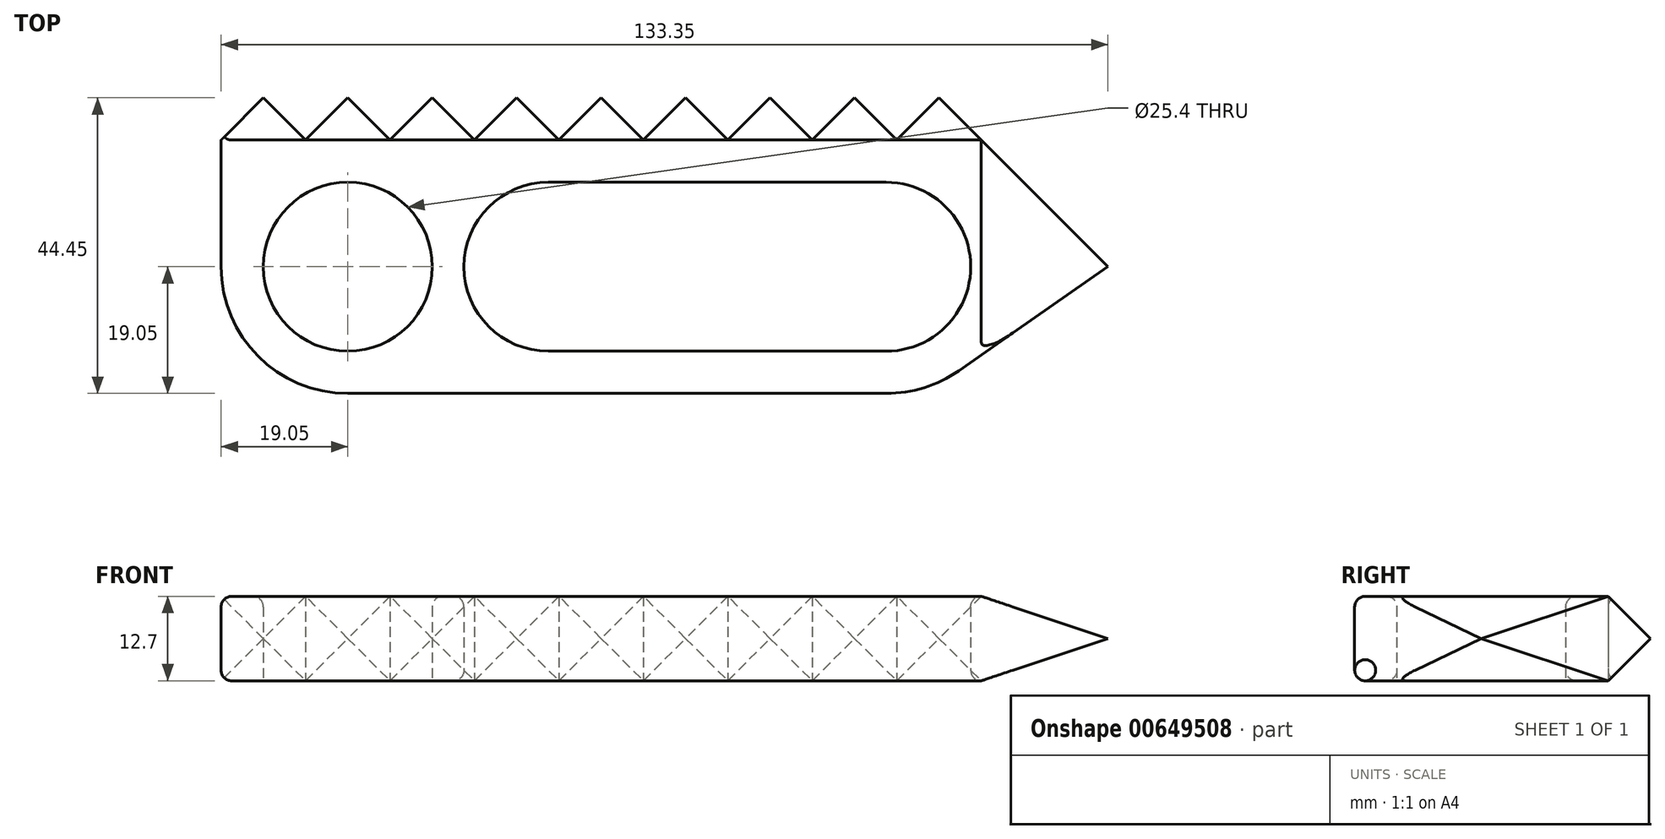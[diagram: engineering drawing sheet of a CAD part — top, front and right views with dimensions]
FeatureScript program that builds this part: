
annotation { "Feature Type Name" : "Feature", "Feature Type Description" : "" }
export const myFeature = defineFeature(function(context is Context, id is Id, definition is map)
    precondition{}
    {
        {
            var Q0;
            Q0=qCreatedBy(makeId("Top.planeOp"),FACE);
            var sketch = newSketch(context, id + "F0", { "sketchPlane" : qUnion([Q0])});
            skCircle(sketch, "E0", {"center": v(0, 0) * mm, "radius": 12.7 * mm});
            skArc(sketch, "E1", {"start": v(30.15, 12.7) * mm, "mid": v(17.46, 0) * mm, "end": v(30.15, -12.7) * mm});
            skLineSegment(sketch, "E2", {"start": v(30.15, 12.7) * mm, "end": v(80.95, 12.7) * mm});
            skLineSegment(sketch, "E3", {"start": v(30.15, -12.7) * mm, "end": v(80.95, -12.7) * mm});
            skArc(sketch, "E4", {"start": v(80.95, -12.7) * mm, "mid": v(93.66, 0) * mm, "end": v(80.95, 12.7) * mm});
            skArc(sketch, "E5", {"start": v(0, -19.05) * mm, "mid": v(-13.47, -13.47) * mm, "end": v(-19.05, 0) * mm});
            skArc(sketch, "E6", {"start": v(80.96, -19.05) * mm, "mid": v(94.43, -13.47) * mm, "end": v(100.01, 0) * mm});
            skLineSegment(sketch, "E7", {"start": v(0, -19.05) * mm, "end": v(80.96, -19.05) * mm});
            skLineSegment(sketch, "E8", {"start": v(-19.05, 0) * mm, "end": v(-19.05, 25.4) * mm});
            skLineSegment(sketch, "E9", {"start": v(100.01, 0) * mm, "end": v(100.01, 25.4) * mm});
            skLineSegment(sketch, "E10", {"start": v(100.01, 25.4) * mm, "end": v(-19.05, 25.4) * mm});
            skLineSegment(sketch, "E11", {"start": v(-19.05, 19.05) * mm, "end": v(100.01, 19.05) * mm});
            skLineSegment(sketch, "E12", {"start": v(-12.7, 25.4) * mm, "end": v(-19.05, 19.05) * mm});
            skLineSegment(sketch, "E13", {"start": v(-12.7, 25.4) * mm, "end": v(-6.35, 19.05) * mm});
            skLineSegment(sketch, "E14", {"start": v(-6.35, 19.05) * mm, "end": v(0, 25.4) * mm});
            skLineSegment(sketch, "E15", {"start": v(0, 25.4) * mm, "end": v(6.35, 19.05) * mm});
            skLineSegment(sketch, "E16", {"start": v(6.35, 19.05) * mm, "end": v(12.7, 25.4) * mm});
            skLineSegment(sketch, "E17", {"start": v(12.7, 25.4) * mm, "end": v(12.7, 25.4) * mm});
            skLineSegment(sketch, "E18", {"start": v(12.7, 25.4) * mm, "end": v(19.05, 19.05) * mm});
            skLineSegment(sketch, "E19", {"start": v(19.05, 19.05) * mm, "end": v(25.4, 25.4) * mm});
            skLineSegment(sketch, "E20", {"start": v(25.4, 25.4) * mm, "end": v(31.75, 19.05) * mm});
            skLineSegment(sketch, "E21", {"start": v(31.75, 19.05) * mm, "end": v(38.1, 25.4) * mm});
            skPoint(sketch, "E21.endSnap0", {"position": v(40.48, 25.4) * mm});
            skLineSegment(sketch, "E22", {"start": v(38.1, 25.4) * mm, "end": v(44.45, 19.05) * mm});
            skLineSegment(sketch, "E23", {"start": v(44.45, 19.05) * mm, "end": v(50.8, 25.4) * mm});
            skLineSegment(sketch, "E24", {"start": v(50.8, 25.4) * mm, "end": v(57.15, 19.05) * mm});
            skLineSegment(sketch, "E25", {"start": v(57.15, 19.05) * mm, "end": v(63.5, 25.4) * mm});
            skLineSegment(sketch, "E26", {"start": v(63.5, 25.4) * mm, "end": v(69.85, 19.05) * mm});
            skLineSegment(sketch, "E27", {"start": v(69.85, 19.05) * mm, "end": v(76.2, 25.4) * mm});
            skLineSegment(sketch, "E28", {"start": v(76.2, 25.4) * mm, "end": v(82.55, 19.05) * mm});
            skLineSegment(sketch, "E29", {"start": v(82.55, 19.05) * mm, "end": v(88.9, 25.4) * mm});
            skLineSegment(sketch, "E30", {"start": v(88.9, 25.4) * mm, "end": v(114.3, 0) * mm});
            skLineSegment(sketch, "E31", {"start": v(114.3, 0) * mm, "end": v(91.85, -15.63) * mm});
            skSolve(sketch);
        }
        {
            var Q0;
            Q0 = qSketchRegion(id + "F0", true);
            extrude(context, id + "F1", {"entities" : qUnion([Q0]), "depth" : 12.7 * mm, "offsetDistance" : 25.4 * mm});
        }
        {
            var Q0;
            {var subQ0=sQuery(id+"F0.wireOp",EDGE,"E18");Q0=makeQuery(id+"F0.imprint","IMPRINT",FACE,{"disambiguationData":[TD([[makeQuery(id+"F0.imprint","IMPRINT",EDGE,{"derivedFrom":subQ0}),1.0]])]});}
            var Q1;
            {var subQ0=sQuery(id+"F0.wireOp",EDGE,"E22");Q1=makeQuery(id+"F0.imprint","IMPRINT",FACE,{"disambiguationData":[TD([[makeQuery(id+"F0.imprint","IMPRINT",EDGE,{"derivedFrom":subQ0}),1.0]])]});}
            var Q2;
            {var subQ3=sQuery(id+"F0.wireOp",EDGE,"E12");Q2=makeQuery(id+"F0.imprint","IMPRINT",FACE,{"disambiguationData":[TD([[makeQuery(id+"F0.imprint","IMPRINT",EDGE,{"derivedFrom":subQ3}),-1.0]])]});}
            var Q3;
            {var subQ0=sQuery(id+"F0.wireOp",EDGE,"E20");Q3=makeQuery(id+"F0.imprint","IMPRINT",FACE,{"disambiguationData":[TD([[makeQuery(id+"F0.imprint","IMPRINT",EDGE,{"derivedFrom":subQ0}),1.0]])]});}
            var Q4;
            {var subQ0=sQuery(id+"F0.wireOp",EDGE,"E10");var subQ1=sQuery(id+"F0.wireOp",EDGE,"E9");var subQ2=makeQuery(id+"F0.imprint","INTERSECT",VERTEX,{"derivedFrom":[subQ1,subQ0]});Q4=makeQuery(id+"F0.imprint","IMPRINT",FACE,{"disambiguationData":[TD([[makeQuery(id+"F0.imprint","IMPRINT",EDGE,{"disambiguationData":[TD([[subQ2,1.0]])],"derivedFrom":subQ1}),1.0]])]});}
            var Q5;
            {var subQ0=sQuery(id+"F0.wireOp",EDGE,"E28");Q5=makeQuery(id+"F0.imprint","IMPRINT",FACE,{"disambiguationData":[TD([[makeQuery(id+"F0.imprint","IMPRINT",EDGE,{"derivedFrom":subQ0}),1.0]])]});}
            var Q6;
            {var subQ0=sQuery(id+"F0.wireOp",EDGE,"E15");Q6=makeQuery(id+"F0.imprint","IMPRINT",FACE,{"disambiguationData":[TD([[makeQuery(id+"F0.imprint","IMPRINT",EDGE,{"derivedFrom":subQ0}),1.0]])]});}
            var Q7;
            {var subQ0=sQuery(id+"F0.wireOp",EDGE,"E24");Q7=makeQuery(id+"F0.imprint","IMPRINT",FACE,{"disambiguationData":[TD([[makeQuery(id+"F0.imprint","IMPRINT",EDGE,{"derivedFrom":subQ0}),1.0]])]});}
            var Q8;
            {var subQ0=sQuery(id+"F0.wireOp",EDGE,"E26");Q8=makeQuery(id+"F0.imprint","IMPRINT",FACE,{"disambiguationData":[TD([[makeQuery(id+"F0.imprint","IMPRINT",EDGE,{"derivedFrom":subQ0}),1.0]])]});}
            var Q9;
            {var subQ0=sQuery(id+"F0.wireOp",EDGE,"E13");Q9=makeQuery(id+"F0.imprint","IMPRINT",FACE,{"disambiguationData":[TD([[makeQuery(id+"F0.imprint","IMPRINT",EDGE,{"derivedFrom":subQ0}),1.0]])]});}
            var Q10;
            {var subQ0=sQuery(id+"F0.wireOp",EDGE,"E11");var subQ1=sQuery(id+"F0.wireOp",EDGE,"E9");var subQ2=makeQuery(id+"F0.imprint","INTERSECT",VERTEX,{"derivedFrom":[subQ1,subQ0]});Q10=makeQuery(id+"F0.imprint","IMPRINT",FACE,{"disambiguationData":[TD([[makeQuery(id+"F0.imprint","IMPRINT",EDGE,{"disambiguationData":[TD([[subQ2,1.0]])],"derivedFrom":subQ1}),1.0]])]});}
            extrude(context, id + "F2", {"entities" : qUnion([Q0, Q1, Q2, Q3, Q4, Q5, Q6, Q7, Q8, Q9, Q10]), "operationType" : NewBodyOperationType.REMOVE, "depth" : 25.4 * mm, "offsetDistance" : 25.4 * mm});
        }
        {
            var Q0;
            Q0=qCreatedBy(makeId("Right.planeOp"),FACE);
            var sketch = newSketch(context, id + "F3", { "sketchPlane" : qUnion([Q0])});
            skPoint(sketch, "E32", {"position": v(25.4, 0) * mm});
            skPoint(sketch, "E33", {"position": v(19.05, 0) * mm});
            skPoint(sketch, "E34", {"position": v(19.05, 12.7) * mm});
            skPoint(sketch, "E35", {"position": v(25.4, 12.7) * mm});
            skLineSegment(sketch, "E36", {"start": v(19.05, 0) * mm, "end": v(25.4, 6.35) * mm});
            skLineSegment(sketch, "E37", {"start": v(25.4, 6.35) * mm, "end": v(19.05, 12.7) * mm});
            skLineSegment(sketch, "E38", {"start": v(19.05, 12.7) * mm, "end": v(25.4, 12.7) * mm});
            skLineSegment(sketch, "E39", {"start": v(25.4, 12.7) * mm, "end": v(25.4, 0) * mm});
            skLineSegment(sketch, "E40", {"start": v(25.4, 0) * mm, "end": v(19.05, 0) * mm});
            skSolve(sketch);
        }
        {
            var Q0;
            Q0 = qSketchRegion(id + "F3", true);
            extrude(context, id + "F4", {"entities" : qUnion([Q0]), "operationType" : NewBodyOperationType.REMOVE, "depth" : 127 * mm, "offsetDistance" : 25.4 * mm, "hasSecondDirection" : true, "secondDirectionOppositeDirection" : true, "secondDirectionDepth" : 25.4 * mm});
        }
        {
            var Q0;
            Q0=qCreatedBy(makeId("Front.planeOp"),FACE);
            var sketch = newSketch(context, id + "F5", { "sketchPlane" : qUnion([Q0])});
            skPoint(sketch, "E41", {"position": v(95.25, 0) * mm});
            skPoint(sketch, "E42", {"position": v(95.25, 12.7) * mm});
            skPoint(sketch, "E43", {"position": v(114.3, 0) * mm});
            skPoint(sketch, "E44", {"position": v(114.3, 12.7) * mm});
            skLineSegment(sketch, "E45", {"start": v(95.25, 0) * mm, "end": v(114.3, 0) * mm});
            skLineSegment(sketch, "E46", {"start": v(114.3, 0) * mm, "end": v(114.3, 12.7) * mm});
            skLineSegment(sketch, "E47", {"start": v(114.3, 12.7) * mm, "end": v(95.25, 12.7) * mm});
            skLineSegment(sketch, "E48", {"start": v(95.25, 12.7) * mm, "end": v(114.3, 6.35) * mm});
            skLineSegment(sketch, "E49", {"start": v(114.3, 6.35) * mm, "end": v(95.25, 0) * mm});
            skSolve(sketch);
        }
        {
            var Q0;
            Q0 = qSketchRegion(id + "F5", true);
            extrude(context, id + "F6", {"entities" : qUnion([Q0]), "operationType" : NewBodyOperationType.REMOVE, "oppositeDirection" : true, "depth" : 50.8 * mm, "offsetDistance" : 25.4 * mm, "hasSecondDirection" : true, "secondDirectionOppositeDirection" : false, "secondDirectionDepth" : 25.4 * mm});
        }
        {
            var Q0;
            Q0=makeQuery(id+"F1.opExtrude","SWEPT_FACE",FACE,{"disambiguationData":[OSD([sQuery(id+"F0.wireOp",EDGE,"E2")])]});
            var Q1;
            Q1=makeQuery(id+"F1.opExtrude","CAP_EDGE",EDGE,{"disambiguationData":[OSD([sQuery(id+"F0.wireOp",EDGE,"E0")])],"isStart":false});
            fillet(context, id + "F7", {"entities" : qUnion([Q0, Q1]), "radius" : 1.59 * mm, "tangentPropagation" : true, "allowEdgeOverflow" : false});
        }
        {
            var Q0;
            Q0=makeQuery(id+"F1.opExtrude","SWEPT_FACE",FACE,{"disambiguationData":[OSD([sQuery(id+"F0.wireOp",EDGE,"E7")])]});
            fillet(context, id + "F8", {"entities" : qUnion([Q0]), "radius" : 1.59 * mm, "tangentPropagation" : true, "allowEdgeOverflow" : false});
        }
    });
